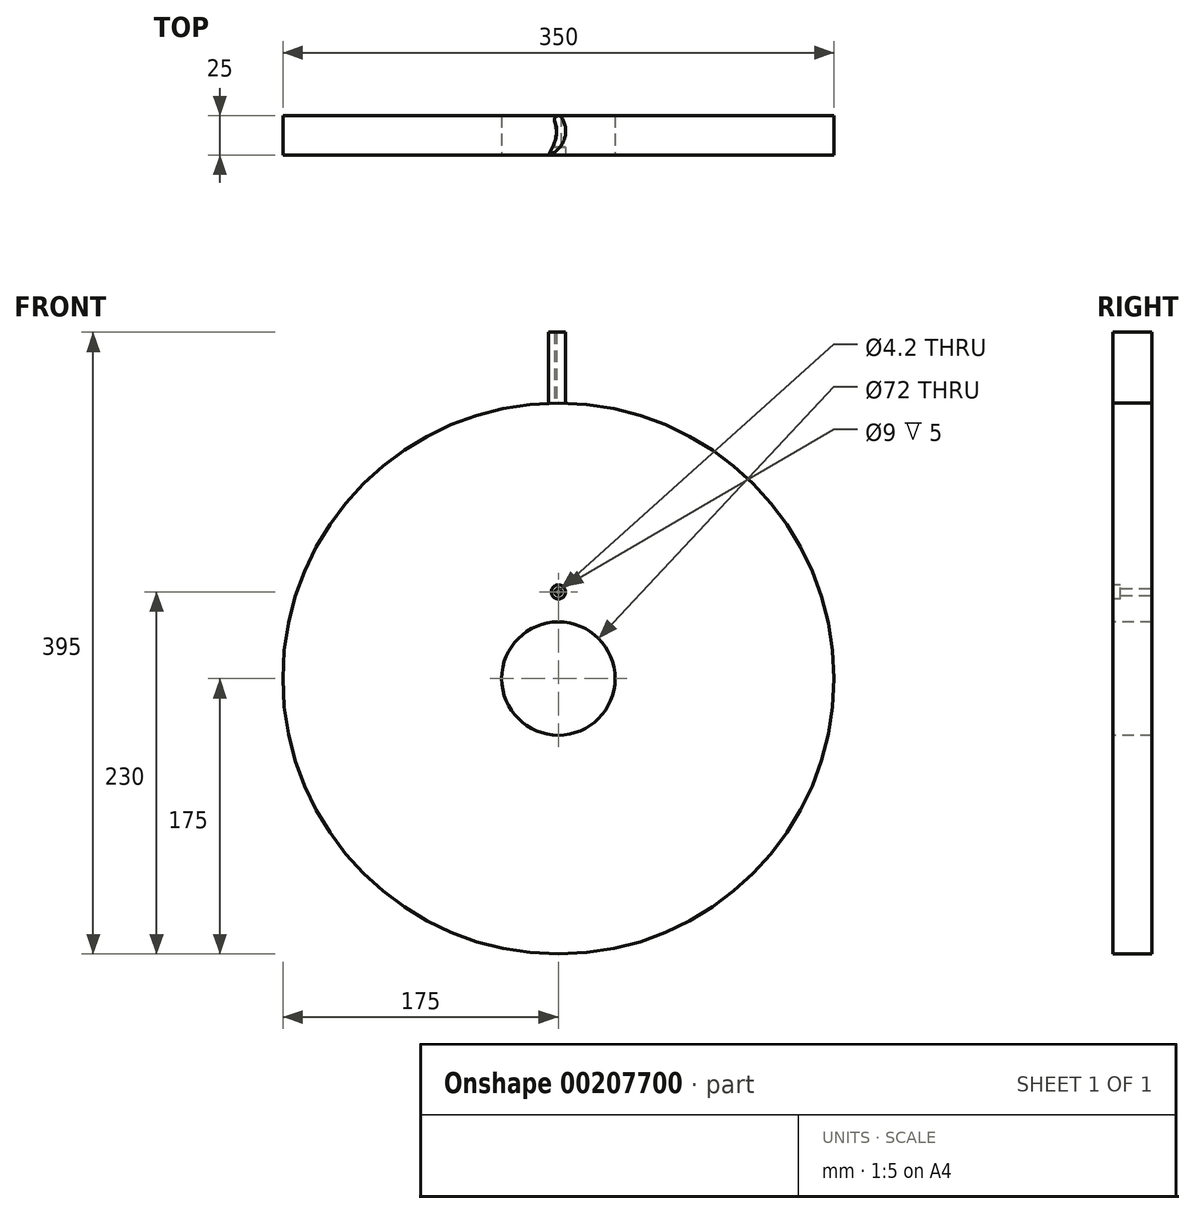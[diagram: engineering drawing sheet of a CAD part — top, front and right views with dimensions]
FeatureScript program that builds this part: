
annotation { "Feature Type Name" : "Feature", "Feature Type Description" : "" }
export const myFeature = defineFeature(function(context is Context, id is Id, definition is map)
    precondition{}
    {
        {
            var Q0;
            Q0=qCreatedBy(makeId("Front.planeOp"),FACE);
            var sketch = newSketch(context, id + "F0", { "sketchPlane" : qUnion([Q0])});
            skCircle(sketch, "E0", {"center": v(0, 0) * mm, "radius": 175 * mm});
            skCircle(sketch, "E1", {"center": v(0, 0) * mm, "radius": 36 * mm, "construction": true});
            skSolve(sketch);
        }
        {
            var Q0;
            Q0 = qSketchRegion(id + "F0", true);
            extrude(context, id + "F1", {"entities" : qUnion([Q0]), "depth" : 25 * mm});
        }
        {
            var Q0;
            Q0=qCreatedBy(makeId("Top.planeOp"),FACE);
            var sketch = newSketch(context, id + "F2", { "sketchPlane" : qUnion([Q0])});
            skLineSegment(sketch, "E2", {"start": v(0, 0) * mm, "end": v(0, -25) * mm, "construction": true});
            skCircle(sketch, "E3", {"center": v(0, -2.5) * mm, "radius": 2.5 * mm});
            skLineSegment(sketch, "E4", {"start": v(0, -2.5) * mm, "end": v(-69.25, -25) * mm, "construction": true});
            skLineSegment(sketch, "E5", {"start": v(0, -2.5) * mm, "end": v(-11.46, -25) * mm, "construction": true});
            skLineSegment(sketch, "E6", {"start": v(0, -12.5) * mm, "end": v(-6.37, -25) * mm, "construction": true});
            skLineSegment(sketch, "E7", {"start": v(0, -22.93) * mm, "end": v(-6.37, -25) * mm, "construction": true});
            skArc(sketch, "E8", {"start": v(-6.37, -25) * mm, "mid": v(3.74, -15.16) * mm, "end": v(2.1, -1.14) * mm});
            skArc(sketch, "E9", {"start": v(-3.18, -18.75) * mm, "mid": v(-1.14, -11.16) * mm, "end": v(-2.34, -3.38) * mm});
            skLineSegment(sketch, "E10", {"start": v(-3.18, -18.75) * mm, "end": v(-6.37, -25) * mm});
            skSolve(sketch);
        }
        {
            var Q0;
            Q0 = qSketchRegion(id + "F2", true);
            extrude(context, id + "F3", {"entities" : qUnion([Q0]), "operationType" : NewBodyOperationType.ADD, "depth" : 220 * mm});
        }
        {
            var Q0;
            Q0=makeQuery(id+"F1.opExtrude","CAP_FACE",FACE,{"disambiguationData":[OSD([sQuery(id+"F0.wireOp",EDGE,"E0")])],"isStart":false});
            var sketch = newSketch(context, id + "F4", { "sketchPlane" : qUnion([Q0])});
            skCircle(sketch, "E11", {"center": v(0, 0) * mm, "radius": 36 * mm});
            skSolve(sketch);
        }
        {
            var Q0;
            Q0 = qSketchRegion(id + "F4", true);
            extrude(context, id + "F5", {"entities" : qUnion([Q0]), "operationType" : NewBodyOperationType.REMOVE, "endBound" : BoundingType.THROUGH_ALL, "oppositeDirection" : true, "depth" : 25 * mm});
        }
        {
            var Q0;
            Q0=makeQuery(id+"F1.opExtrude","CAP_FACE",FACE,{"disambiguationData":[OSD([sQuery(id+"F0.wireOp",EDGE,"E0")])],"isStart":true});
            var sketch = newSketch(context, id + "F6", { "sketchPlane" : qUnion([Q0])});
            skCircle(sketch, "E12", {"center": v(0, 55) * mm, "radius": 2.5 * mm});
            skSolve(sketch);
        }
        {
            var Q0;
            Q0=sQuery(id+"F6.wireOp",VERTEX,"E12.center");
            var Q1;
            Q1=makeQuery(id+"F1.opExtrude","SWEPT_BODY",BODY,{"disambiguationData":[OSD([sQuery(id+"F0.wireOp",EDGE,"E0")])]});
            hole(context, id + "F7", {"style" : HoleStyle.SIMPLE, "endStyle" : HoleEndStyle.THROUGH, "standardTappedOrClearance" : lookupTablePath({ "standard" : "ISO", "engagement" : "75%", "pitch" : "0.8 mm", "size" : "M5", "type" : "Tapped" }), "standardBlindInLast" : lookupTablePath({ "standard" : "ISO", "engagement" : "75%", "pitch" : "0.8 mm", "size" : "M5", "type" : "Tapped" }), "holeDiameter" : 4.2 * mm, "showTappedDepth" : true, "tappedDepth" : 12.5 * mm, "tapClearance" : 3, "locations" : qUnion([Q0]), "scope" : qUnion([Q1]), "majorDiameter" : 5 * mm});
        }
        {
            var Q0;
            Q0=makeQuery(id+"F1.opExtrude","CAP_FACE",FACE,{"disambiguationData":[OSD([sQuery(id+"F0.wireOp",EDGE,"E0")])],"isStart":false});
            var sketch = newSketch(context, id + "F8", { "sketchPlane" : qUnion([Q0])});
            skCircle(sketch, "E13", {"center": v(0, 55) * mm, "radius": 4.5 * mm});
            skSolve(sketch);
        }
        {
            var Q0;
            Q0 = qSketchRegion(id + "F8", true);
            extrude(context, id + "F9", {"entities" : qUnion([Q0]), "operationType" : NewBodyOperationType.REMOVE, "oppositeDirection" : true, "depth" : 5 * mm});
        }
    });
